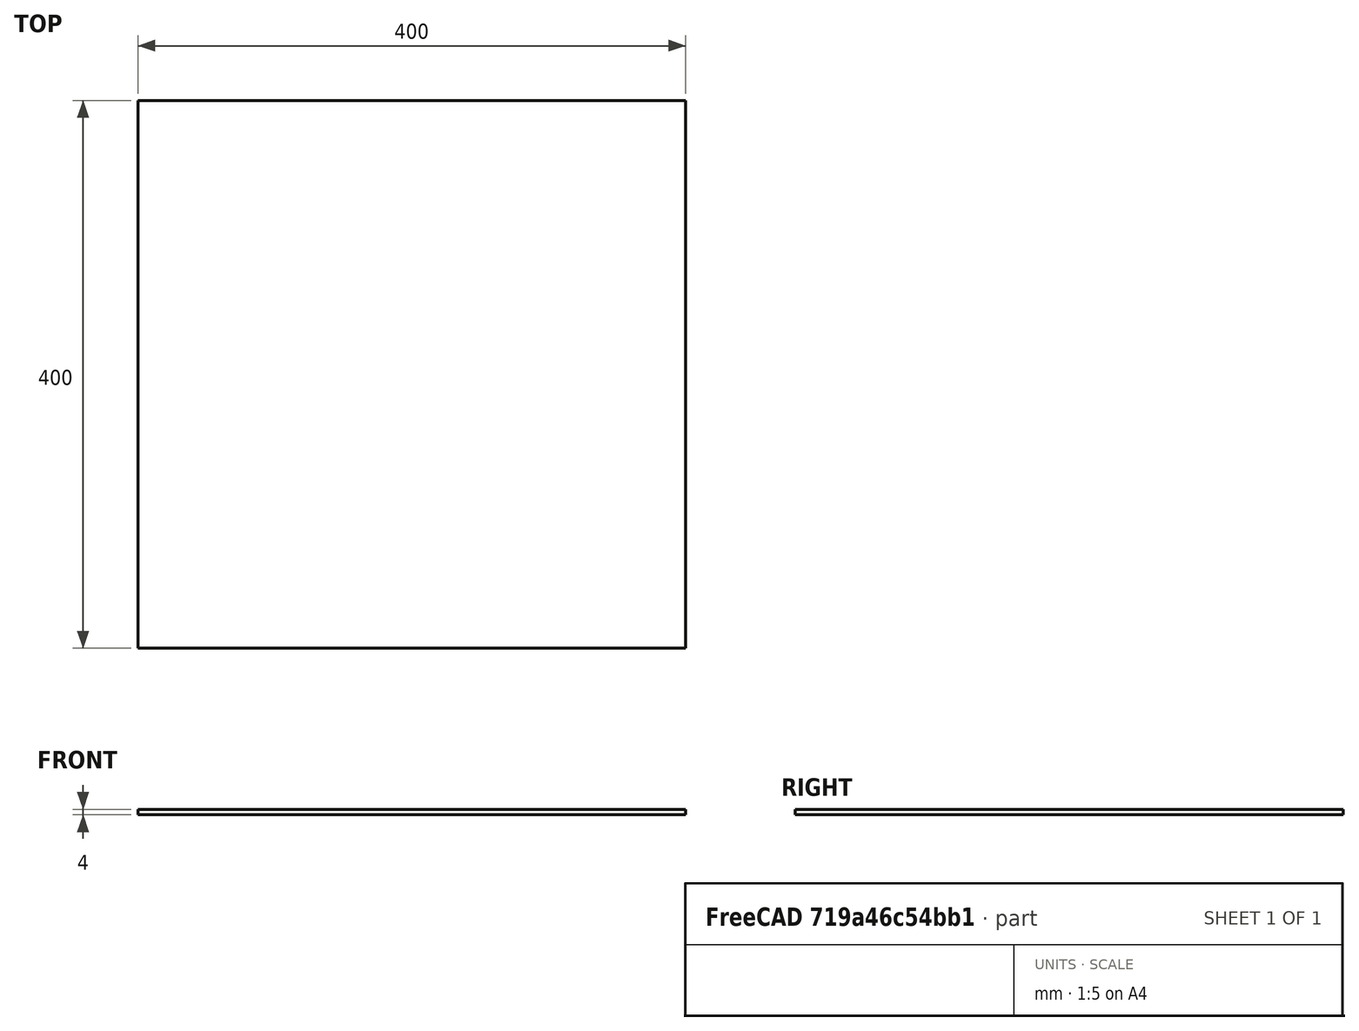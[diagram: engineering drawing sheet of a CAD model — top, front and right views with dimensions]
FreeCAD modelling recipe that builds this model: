
FCSTD DOCUMENT  (FreeCAD 0.15R4671 (Git))
Label: Plexiglas_front
License: All rights reserved
LicenseURL: http://en.wikipedia.org/wiki/All_rights_reserved
objects: Sketcher::SketchObject×1, PartDesign::Pad×1
note: 3 computed .brp shape members not serialized (recipe doc carries the construction recipe); baked Part::Feature solids carry a one-line shape summary decoded from their .brp

FEATURE [Sketcher::SketchObject] Sketch
  sketch-geometry (4):
    g0: LineSegment StartX=-200 StartY=200 StartZ=0 EndX=200 EndY=200 EndZ=0
    g1: LineSegment StartX=200 StartY=200 StartZ=0 EndX=200 EndY=-200 EndZ=0
    g2: LineSegment StartX=200 StartY=-200 StartZ=0 EndX=-200 EndY=-200 EndZ=0
    g3: LineSegment StartX=-200 StartY=-200 StartZ=0 EndX=-200 EndY=200 EndZ=0
  constraints (12):
    c: Coincident(g0,g1)
    c: Coincident(g1,g2)
    c: Coincident(g2,g3)
    c: Coincident(g3,g0)
    c: Horizontal(g0)
    c: Horizontal(g2)
    c: Vertical(g1)
    c: Vertical(g3)
    c: Symmetric(g0,g2,g-1)
    c: Symmetric(g0,g0,g-2)
    c: Distance(g0) = 400
    c: Distance(g1) = 400
FEATURE [PartDesign::Pad] Pad
  Length = 4
  Length2 = 100
  Sketch = -> Sketch
  Type = 0
